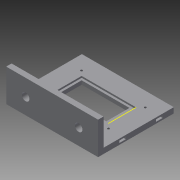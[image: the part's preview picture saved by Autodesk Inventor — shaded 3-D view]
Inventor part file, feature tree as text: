
AUTODESK INVENTOR PART (.ipt)
format: ipt  version: 2015 (Build 190159000, 159)  size: 189,440 bytes
history: native  units: in
note: dims shown in document units (in); Inventor stores cm internally (conversion verified against a paired STEP export)
features: sketch x9, extrude x8
ambient origin geometry x8: Origin, YZ Plane, XZ Plane, XY Plane, X Axis, Y Axis, Z Axis, Center Point
bodies: Solid1 (feature_tree)
feature tree (17):
  extrude  "Extrusion1"  Depth=3.3465in
  extrude  "Extrusion2"  TaperAngle=0.0deg  [1 undecoded]
  extrude  "Extrusion3"  Depth=0.1969in
  extrude  "Extrusion4"  Depth=0.685in
  extrude  "Extrusion9"  Depth=0.8622in
  sketch  "Sketch16"  dims[d18=0.0591in d19=0.0in d20=0.0787in]
  extrude  "Extrusion14"  Depth=0.0787in
  extrude  "Extrusion16"  Depth=0.0787in
  extrude  "Extrusion17"  Depth=0.0394in TaperAngle=0.0deg
  sketch  "Sketch1"  dims[d4=2.7559in d5=3.3465in]
  sketch  "Sketch2"  dims[d6=1.1811in d7=0.0in d8=0.0in]
  sketch  "Sketch3"  dims[d9=0.0in d10=0.1969in]
  sketch  "Sketch4"  dims[d12=0.9843in d13=0.0in d14=0.685in]
  sketch  "Sketch10"  dims[d15=0.685in d17=0.8622in]
  sketch  "Sketch17"  dims[d21=0.0787in d22=0.0787in]
  sketch  "Sketch20"  dims[d23=0.1575in d24=0.0394in d25=0.0in]
  sketch  "Sketch21"  dims[d53=0.6004in d55=0.6004in d58=0.2756in d59=0.2756in d60=0.1969in d61=0.0in d70=1.9291in d71=0.7087in d93=0.0in d94=0.0in d95=0.0in d96=0.0in d97=0.1969in d98=0.0in d106=1.0039in d107=0.0787in d110=1.3386in d111=2.3228in d113=0.0787in d119=0.0787in d124=0.2362in d125=0.2362in d128=0.0787in d129=0.0787in d130=0.6299in d131=0.0in d136=0.6299in d137=0.0in]
note: 1 required parameter value undecoded (feature->parameter linkage not recoverable at this tier; creation-order binding heuristic only, values carry confidence <= 0.55)
